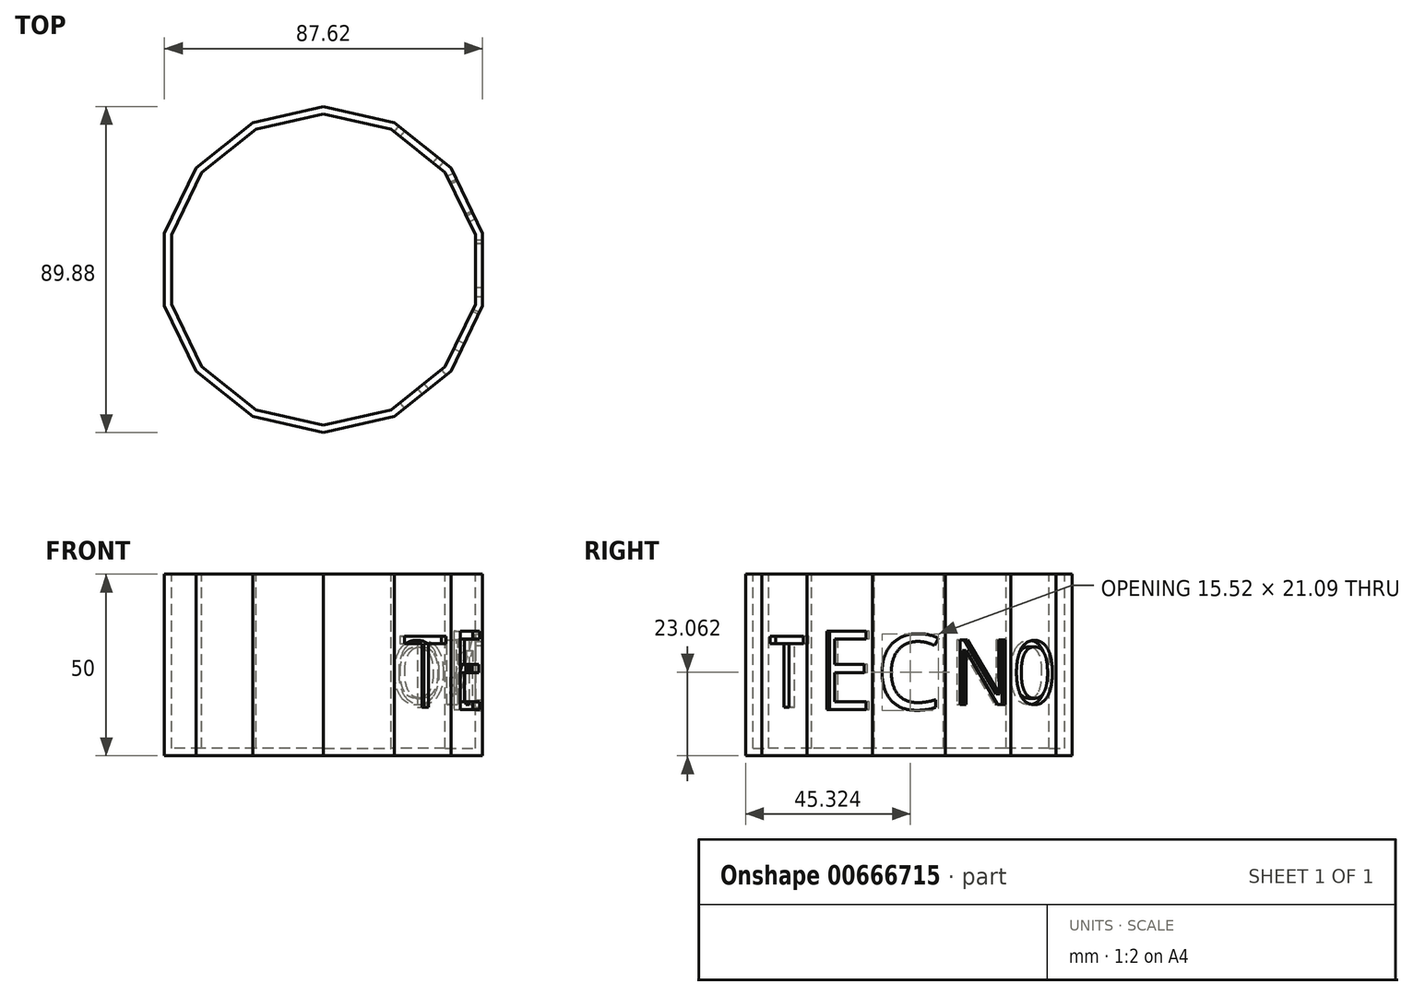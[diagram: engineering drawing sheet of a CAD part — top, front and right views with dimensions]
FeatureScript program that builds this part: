
annotation { "Feature Type Name" : "Feature", "Feature Type Description" : "" }
export const myFeature = defineFeature(function(context is Context, id is Id, definition is map)
    precondition{}
    {
        {
            var Q0;
            Q0=qCreatedBy(makeId("Top.planeOp"),FACE);
            var sketch = newSketch(context, id + "F0", { "sketchPlane" : qUnion([Q0])});
            skCircle(sketch, "E0.cCircle", {"center": v(0, 0) * mm, "radius": 44.94 * mm, "construction": true});
            skLineSegment(sketch, "E0.0", {"start": v(0, -44.94) * mm, "end": v(-19.5, -40.49) * mm});
            skLineSegment(sketch, "E0.1", {"start": v(-19.5, -40.49) * mm, "end": v(-35.14, -28.02) * mm});
            skLineSegment(sketch, "E0.2", {"start": v(-35.14, -28.02) * mm, "end": v(-43.81, -10) * mm});
            skLineSegment(sketch, "E0.3", {"start": v(-43.81, -10) * mm, "end": v(-43.81, 10) * mm});
            skLineSegment(sketch, "E0.4", {"start": v(-43.81, 10) * mm, "end": v(-35.14, 28.02) * mm});
            skLineSegment(sketch, "E0.5", {"start": v(-35.14, 28.02) * mm, "end": v(-19.5, 40.49) * mm});
            skLineSegment(sketch, "E0.6", {"start": v(-19.5, 40.49) * mm, "end": v(0, 44.94) * mm});
            skLineSegment(sketch, "E0.7", {"start": v(0, 44.94) * mm, "end": v(19.5, 40.49) * mm});
            skLineSegment(sketch, "E0.8", {"start": v(19.5, 40.49) * mm, "end": v(35.14, 28.02) * mm});
            skLineSegment(sketch, "E0.9", {"start": v(35.14, 28.02) * mm, "end": v(43.81, 10) * mm});
            skLineSegment(sketch, "E0.10", {"start": v(43.81, 10) * mm, "end": v(43.81, -10) * mm});
            skLineSegment(sketch, "E0.11", {"start": v(43.81, -10) * mm, "end": v(35.14, -28.02) * mm});
            skLineSegment(sketch, "E0.12", {"start": v(35.14, -28.02) * mm, "end": v(19.5, -40.49) * mm});
            skLineSegment(sketch, "E0.13", {"start": v(19.5, -40.49) * mm, "end": v(0, -44.94) * mm});
            skSolve(sketch);
        }
        {
            var Q0;
            Q0=qCreatedBy(makeId("Top.planeOp"),FACE);
            cPlane(context, id + "F1", {"entities" : qUnion([Q0]), "cplaneType" : CPlaneType.OFFSET, "offset" : 50 * mm, "width" : 150 * mm, "height" : 150 * mm});
        }
        {
            var Q0;
            Q0=qCreatedBy(id+"F1.planeOp",FACE);
            var sketch = newSketch(context, id + "F2", { "sketchPlane" : qUnion([Q0])});
            skCircle(sketch, "E1.cCircle", {"center": v(0, 0) * mm, "radius": 44.94 * mm, "construction": true});
            skLineSegment(sketch, "E1.0", {"start": v(0, 44.94) * mm, "end": v(19.5, 40.49) * mm});
            skLineSegment(sketch, "E1.1", {"start": v(19.5, 40.49) * mm, "end": v(35.14, 28.02) * mm});
            skLineSegment(sketch, "E1.2", {"start": v(35.14, 28.02) * mm, "end": v(43.81, 10) * mm});
            skLineSegment(sketch, "E1.3", {"start": v(43.81, 10) * mm, "end": v(43.81, -10) * mm});
            skLineSegment(sketch, "E1.4", {"start": v(43.81, -10) * mm, "end": v(35.14, -28.02) * mm});
            skLineSegment(sketch, "E1.5", {"start": v(35.14, -28.02) * mm, "end": v(19.5, -40.49) * mm});
            skLineSegment(sketch, "E1.6", {"start": v(19.5, -40.49) * mm, "end": v(0, -44.94) * mm});
            skLineSegment(sketch, "E1.7", {"start": v(0, -44.94) * mm, "end": v(-19.5, -40.49) * mm});
            skLineSegment(sketch, "E1.8", {"start": v(-19.5, -40.49) * mm, "end": v(-35.14, -28.02) * mm});
            skLineSegment(sketch, "E1.9", {"start": v(-35.14, -28.02) * mm, "end": v(-43.81, -10) * mm});
            skLineSegment(sketch, "E1.10", {"start": v(-43.81, -10) * mm, "end": v(-43.81, 10) * mm});
            skLineSegment(sketch, "E1.11", {"start": v(-43.81, 10) * mm, "end": v(-35.14, 28.02) * mm});
            skLineSegment(sketch, "E1.12", {"start": v(-35.14, 28.02) * mm, "end": v(-19.5, 40.49) * mm});
            skLineSegment(sketch, "E1.13", {"start": v(-19.5, 40.49) * mm, "end": v(0, 44.94) * mm});
            skSolve(sketch);
        }
        {
            var Q0;
            Q0=makeQuery(id+"F0.imprint","IMPRINT",FACE,{"disambiguationData":[TD([[makeQuery(id+"F0.imprint","IMPRINT",EDGE,{"derivedFrom":sQuery(id+"F0.wireOp",EDGE,"E0.0")}),-1.0]])]});
            var Q1;
            Q1=makeQuery(id+"F2.imprint","IMPRINT",FACE,{"disambiguationData":[TD([[makeQuery(id+"F2.imprint","IMPRINT",EDGE,{"derivedFrom":sQuery(id+"F2.wireOp",EDGE,"E1.0")}),-1.0]])]});
            loft(context, id + "F3", {"sheetProfilesArray" : [{ "sheetProfileEntities" : qUnion([Q0]) }, { "sheetProfileEntities" : qUnion([Q1]) }]});
        }
        {
            var Q0;
            Q0=makeQuery(id+"F3.opLoft","CAP_FACE",FACE,{"disambiguationData":[OSD([makeQuery(id+"F2.imprint","IMPRINT",FACE,{"disambiguationData":[TD([[makeQuery(id+"F2.imprint","IMPRINT",EDGE,{"derivedFrom":sQuery(id+"F2.wireOp",EDGE,"E1.0")}),-1.0]])]})])],"isStart":true});
            shell(context, id + "F4", {"entities" : qUnion([Q0]), "thickness" : 2 * mm});
        }
        {
            var Q0;
            Q0=makeQuery(id+"F3.opLoft","SWEPT_FACE",FACE,{"disambiguationData":[OSD([sQuery(id+"F0.wireOp",EDGE,"E0.10"),sQuery(id+"F0.wireOp",EDGE,"E0.11"),sQuery(id+"F0.wireOp",EDGE,"E0.12"),sQuery(id+"F2.wireOp",EDGE,"E1.3"),sQuery(id+"F2.wireOp",EDGE,"E1.4"),sQuery(id+"F2.wireOp",EDGE,"E1.5")])]});
            var sketch = newSketch(context, id + "F5", { "sketchPlane" : qUnion([Q0])});
            skText(sketch, "E2", { "text": "E", "fontName": "OpenSans-Regular.ttf"});
            const initialGuessF5  = {"E2": [-0.00703, 0.01267, 1, 0, 0.02186]};
            skSetInitialGuess(sketch, initialGuessF5);
            skSolve(sketch);
        }
        {
            var Q0;
            Q0 = qSketchRegion(id + "F5", true);
            extrude(context, id + "F6", {"entities" : qUnion([Q0]), "operationType" : NewBodyOperationType.REMOVE, "oppositeDirection" : true, "depth" : 25 * mm, "offsetDistance" : 25 * mm});
        }
        {
            var Q0;
            Q0=makeQuery(id+"F3.opLoft","SWEPT_FACE",FACE,{"disambiguationData":[OSD([sQuery(id+"F0.wireOp",EDGE,"E0.9"),sQuery(id+"F0.wireOp",EDGE,"E0.10"),sQuery(id+"F0.wireOp",EDGE,"E0.11"),sQuery(id+"F2.wireOp",EDGE,"E1.2"),sQuery(id+"F2.wireOp",EDGE,"E1.3"),sQuery(id+"F2.wireOp",EDGE,"E1.4")])]});
            var sketch = newSketch(context, id + "F7", { "sketchPlane" : qUnion([Q0])});
            skText(sketch, "E3", { "text": "C\n", "fontName": "OpenSans-Regular.ttf"});
            const initialGuessF7  = {"E3": [-0.00913, 0.0128, 1, 0, 0.02069]};
            skSetInitialGuess(sketch, initialGuessF7);
            skSolve(sketch);
        }
        {
            var Q0;
            Q0 = qSketchRegion(id + "F7", true);
            extrude(context, id + "F8", {"entities" : qUnion([Q0]), "operationType" : NewBodyOperationType.REMOVE, "oppositeDirection" : true, "depth" : 25 * mm, "offsetDistance" : 25 * mm});
        }
        {
            var Q0;
            Q0=makeQuery(id+"F3.opLoft","SWEPT_FACE",FACE,{"disambiguationData":[OSD([sQuery(id+"F0.wireOp",EDGE,"E0.8"),sQuery(id+"F0.wireOp",EDGE,"E0.9"),sQuery(id+"F0.wireOp",EDGE,"E0.10"),sQuery(id+"F2.wireOp",EDGE,"E1.1"),sQuery(id+"F2.wireOp",EDGE,"E1.2"),sQuery(id+"F2.wireOp",EDGE,"E1.3")])]});
            var sketch = newSketch(context, id + "F9", { "sketchPlane" : qUnion([Q0])});
            skText(sketch, "E4", { "text": "N", "fontName": "OpenSans-Regular.ttf"});
            const initialGuessF9  = {"E4": [-0.00793, 0.01407, 1, 0, 0.01792]};
            skSetInitialGuess(sketch, initialGuessF9);
            skSolve(sketch);
        }
        {
            var Q0;
            Q0 = qSketchRegion(id + "F9", true);
            extrude(context, id + "F10", {"entities" : qUnion([Q0]), "operationType" : NewBodyOperationType.REMOVE, "oppositeDirection" : true, "depth" : 25 * mm, "offsetDistance" : 25 * mm});
        }
        {
            var Q0;
            Q0=makeQuery(id+"F3.opLoft","SWEPT_FACE",FACE,{"disambiguationData":[OSD([sQuery(id+"F0.wireOp",EDGE,"E0.7"),sQuery(id+"F0.wireOp",EDGE,"E0.8"),sQuery(id+"F0.wireOp",EDGE,"E0.9"),sQuery(id+"F2.wireOp",EDGE,"E1.0"),sQuery(id+"F2.wireOp",EDGE,"E1.1"),sQuery(id+"F2.wireOp",EDGE,"E1.2")])]});
            var sketch = newSketch(context, id + "F11", { "sketchPlane" : qUnion([Q0])});
            skText(sketch, "E5", { "text": "O\n", "fontName": "OpenSans-Regular.ttf"});
            const initialGuessF11  = {"E5": [-0.00887, 0.01431, 1, 0, 0.01736]};
            skSetInitialGuess(sketch, initialGuessF11);
            skSolve(sketch);
        }
        {
            var Q0;
            Q0 = qSketchRegion(id + "F11", true);
            extrude(context, id + "F12", {"entities" : qUnion([Q0]), "operationType" : NewBodyOperationType.REMOVE, "oppositeDirection" : true, "depth" : 25 * mm, "offsetDistance" : 25 * mm});
        }
        {
            var Q0;
            Q0=makeQuery(id+"F3.opLoft","SWEPT_FACE",FACE,{"disambiguationData":[OSD([sQuery(id+"F0.wireOp",EDGE,"E0.11"),sQuery(id+"F0.wireOp",EDGE,"E0.12"),sQuery(id+"F0.wireOp",EDGE,"E0.13"),sQuery(id+"F2.wireOp",EDGE,"E1.4"),sQuery(id+"F2.wireOp",EDGE,"E1.5"),sQuery(id+"F2.wireOp",EDGE,"E1.6")])]});
            var sketch = newSketch(context, id + "F13", { "sketchPlane" : qUnion([Q0])});
            skText(sketch, "E6", { "text": "T", "fontName": "OpenSans-Regular.ttf"});
            const initialGuessF13  = {"E6": [-0.0067, 0.01335, 1, 0, 0.01976]};
            skSetInitialGuess(sketch, initialGuessF13);
            skSolve(sketch);
        }
        {
            var Q0;
            Q0 = qSketchRegion(id + "F13", true);
            extrude(context, id + "F14", {"entities" : qUnion([Q0]), "operationType" : NewBodyOperationType.REMOVE, "oppositeDirection" : true, "depth" : 25 * mm, "offsetDistance" : 25 * mm});
        }
    });
